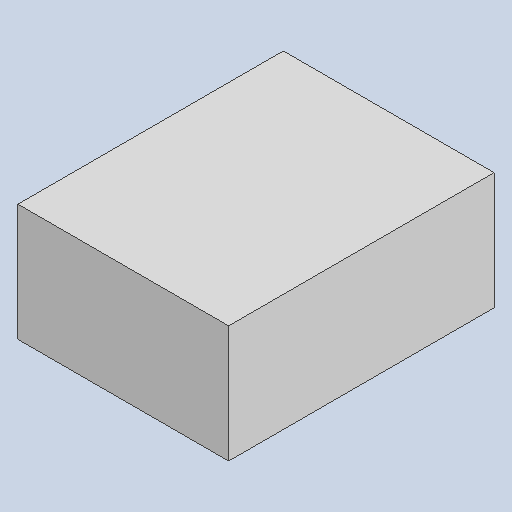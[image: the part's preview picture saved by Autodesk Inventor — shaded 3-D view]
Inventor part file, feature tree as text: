
AUTODESK INVENTOR PART (.ipt)
format: ipt  version: 2022.3 (Build 263350000, 350)  size: 89,088 bytes
history: native  units: mm
features: extrude x1, sketch x1
ambient origin geometry x8: Origin, YZ Plane, XZ Plane, XY Plane, X Axis, Y Axis, Z Axis, Center Point
bodies: Solid1 (feature_tree)
feature tree (2):
  extrude  "Extrusion1"  Depth=3.4mm
  sketch  "Sketch1"  dims[d0=2.7mm d1=3.4mm d2=1.5mm d3=0.0mm]
